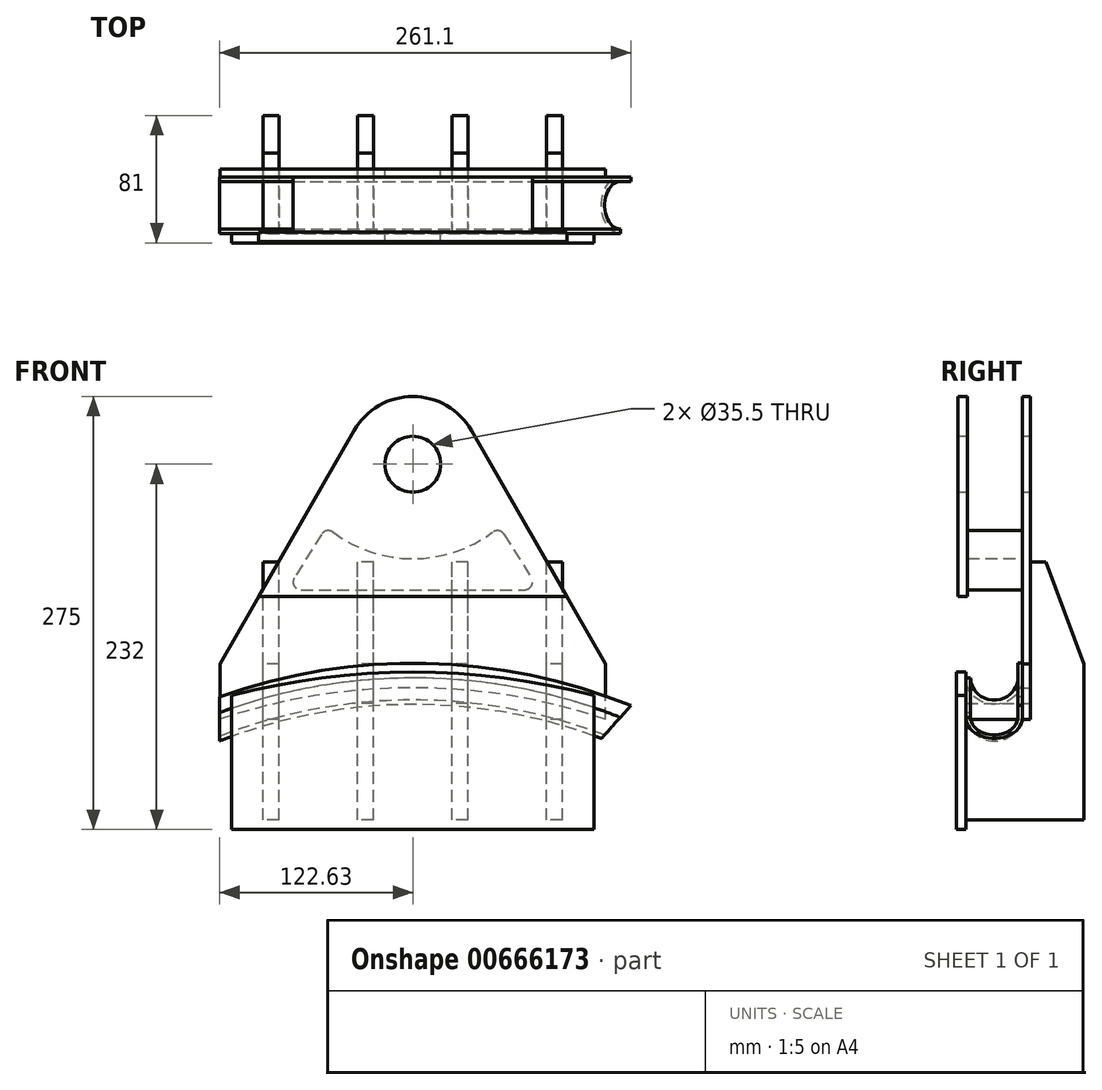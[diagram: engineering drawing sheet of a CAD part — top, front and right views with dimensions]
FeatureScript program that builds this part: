
annotation { "Feature Type Name" : "Feature", "Feature Type Description" : "" }
export const myFeature = defineFeature(function(context is Context, id is Id, definition is map)
    precondition{}
    {
        {
            var Q0;
            Q0=qCreatedBy(makeId("Front.planeOp"),FACE);
            var sketch = newSketch(context, id + "F0", { "sketchPlane" : qUnion([Q0])});
            skLineSegment(sketch, "E0", {"start": v(0, 0) * mm, "end": v(230, 0) * mm});
            skLineSegment(sketch, "E1", {"start": v(230, 0) * mm, "end": v(230, 85) * mm});
            skLineSegment(sketch, "E2", {"start": v(0, 0) * mm, "end": v(0, 85) * mm});
            skLineSegment(sketch, "E3", {"start": v(115, 0) * mm, "end": v(115, 100) * mm, "construction": true});
            skArc(sketch, "E4", {"start": v(230, 85) * mm, "mid": v(115, 100) * mm, "end": v(0, 85) * mm});
            skSolve(sketch);
        }
        {
            var Q0;
            Q0 = qSketchRegion(id + "F0", true);
            extrude(context, id + "F1", {"entities" : qUnion([Q0]), "oppositeDirection" : true, "depth" : 6 * mm, "offsetDistance" : 25 * mm});
        }
        {
            var Q0;
            Q0=qCreatedBy(makeId("Top.planeOp"),FACE);
            var sketch = newSketch(context, id + "F2", { "sketchPlane" : qUnion([Q0])});
            skLineSegment(sketch, "E5.0", {"start": v(0, 6) * mm, "end": v(230, 6) * mm});
            skLineSegment(sketch, "E6", {"start": v(0, 6) * mm, "end": v(0, 81) * mm});
            skLineSegment(sketch, "E7", {"start": v(0, 81) * mm, "end": v(230, 81) * mm});
            skLineSegment(sketch, "E8", {"start": v(230, 81) * mm, "end": v(230, 6) * mm});
            skSolve(sketch);
        }
        {
            var Q0;
            Q0 = qSketchRegion(id + "F2", true);
            extrude(context, id + "F3", {"entities" : qUnion([Q0]), "depth" : 230 * mm, "offsetDistance" : 25 * mm});
        }
        {
            var Q0;
            Q0=makeQuery(id+"F3.opExtrude","SWEPT_FACE",FACE,{"disambiguationData":[OSD([sQuery(id+"F2.wireOp",EDGE,"E6")])]});
            var sketch = newSketch(context, id + "F4", { "sketchPlane" : qUnion([Q0])});
            skLineSegment(sketch, "E9", {"start": v(-47, 230) * mm, "end": v(-47, 70) * mm});
            skLineSegment(sketch, "E10", {"start": v(-47, 70) * mm, "end": v(-6, 70) * mm});
            skLineSegment(sketch, "E11", {"start": v(-6, 70) * mm, "end": v(-6, 230) * mm});
            skLineSegment(sketch, "E12", {"start": v(-6, 230) * mm, "end": v(-47, 230) * mm});
            skSolve(sketch);
        }
        {
            var Q0;
            Q0 = qSketchRegion(id + "F4", true);
            extrude(context, id + "F5", {"entities" : qUnion([Q0]), "operationType" : NewBodyOperationType.REMOVE, "endBound" : BoundingType.THROUGH_ALL, "oppositeDirection" : true, "depth" : 25 * mm, "offsetDistance" : 25 * mm});
        }
        {
            var Q0;
            Q0=makeQuery(id+"F3.opExtrude","CAP_FACE",FACE,{"disambiguationData":[OSD([sQuery(id+"F2.wireOp",EDGE,"E5.0"),sQuery(id+"F2.wireOp",EDGE,"E6"),sQuery(id+"F2.wireOp",EDGE,"E7"),sQuery(id+"F2.wireOp",EDGE,"E8")])],"isStart":false});
            var sketch = newSketch(context, id + "F6", { "sketchPlane" : qUnion([Q0])});
            skLineSegment(sketch, "E13.0", {"start": v(230, 6) * mm, "end": v(0, 6) * mm, "construction": true});
            skLineSegment(sketch, "E14.bottom", {"start": v(0, 81) * mm, "end": v(20, 81) * mm});
            skLineSegment(sketch, "E14.top", {"start": v(0, 6) * mm, "end": v(20, 6) * mm});
            skLineSegment(sketch, "E14.left", {"start": v(0, 81) * mm, "end": v(0, 6) * mm});
            skLineSegment(sketch, "E14.right", {"start": v(20, 81) * mm, "end": v(20, 6) * mm});
            skLineSegment(sketch, "E15.bottom", {"start": v(30, 81) * mm, "end": v(80, 81) * mm});
            skLineSegment(sketch, "E15.top", {"start": v(30, 6) * mm, "end": v(80, 6) * mm});
            skLineSegment(sketch, "E15.left", {"start": v(30, 81) * mm, "end": v(30, 6) * mm});
            skLineSegment(sketch, "E15.right", {"start": v(80, 81) * mm, "end": v(80, 6) * mm});
            skLineSegment(sketch, "E16.bottom", {"start": v(90, 81) * mm, "end": v(140, 81) * mm});
            skLineSegment(sketch, "E16.top", {"start": v(90, 6) * mm, "end": v(140, 6) * mm});
            skLineSegment(sketch, "E16.left", {"start": v(90, 81) * mm, "end": v(90, 6) * mm});
            skLineSegment(sketch, "E16.right", {"start": v(140, 81) * mm, "end": v(140, 6) * mm});
            skLineSegment(sketch, "E17.bottom", {"start": v(150, 81) * mm, "end": v(200, 81) * mm});
            skLineSegment(sketch, "E17.top", {"start": v(150, 6) * mm, "end": v(200, 6) * mm});
            skLineSegment(sketch, "E17.left", {"start": v(150, 81) * mm, "end": v(150, 6) * mm});
            skLineSegment(sketch, "E17.right", {"start": v(200, 81) * mm, "end": v(200, 6) * mm});
            skLineSegment(sketch, "E18.bottom", {"start": v(210, 81) * mm, "end": v(230, 81) * mm});
            skLineSegment(sketch, "E18.top", {"start": v(210, 6) * mm, "end": v(230, 6) * mm});
            skLineSegment(sketch, "E18.left", {"start": v(210, 81) * mm, "end": v(210, 6) * mm});
            skLineSegment(sketch, "E18.right", {"start": v(230, 81) * mm, "end": v(230, 6) * mm});
            skSolve(sketch);
        }
        {
            var Q0;
            Q0 = qSketchRegion(id + "F6", true);
            extrude(context, id + "F7", {"entities" : qUnion([Q0]), "operationType" : NewBodyOperationType.REMOVE, "endBound" : BoundingType.THROUGH_ALL, "oppositeDirection" : true, "depth" : 25 * mm, "offsetDistance" : 25 * mm});
        }
        {
            var Q0;
            Q0=makeQuery(id+"F7.boolean.opBoolean","COPY",FACE,{"derivedFrom":makeQuery(id+"F7.opExtrude","SWEPT_FACE",FACE,{"disambiguationData":[OSD([sQuery(id+"F6.wireOp",EDGE,"E14.right")])]})});
            var sketch = newSketch(context, id + "F8", { "sketchPlane" : qUnion([Q0])});
            skLineSegment(sketch, "E19", {"start": v(-47, 170) * mm, "end": v(-47, 230) * mm});
            skLineSegment(sketch, "E20", {"start": v(-47, 230) * mm, "end": v(-81, 230) * mm});
            skLineSegment(sketch, "E21", {"start": v(-81, 230) * mm, "end": v(-81, 105) * mm});
            skLineSegment(sketch, "E22.0", {"start": v(-81, 0) * mm, "end": v(-6, 0) * mm, "construction": true});
            skLineSegment(sketch, "E23", {"start": v(-81, 105) * mm, "end": v(-57, 170) * mm});
            skLineSegment(sketch, "E24", {"start": v(-57, 170) * mm, "end": v(-47, 170) * mm});
            skLineSegment(sketch, "E25.bottom", {"start": v(-81, 0) * mm, "end": v(-6, 0) * mm});
            skLineSegment(sketch, "E25.top", {"start": v(-81, 6) * mm, "end": v(-6, 6) * mm});
            skLineSegment(sketch, "E25.left", {"start": v(-81, 0) * mm, "end": v(-81, 6) * mm});
            skLineSegment(sketch, "E25.right", {"start": v(-6, 0) * mm, "end": v(-6, 6) * mm});
            skSolve(sketch);
        }
        {
            var Q0;
            Q0=makeQuery(id+"F8.imprint","IMPRINT",FACE,{"disambiguationData":[TD([[makeQuery(id+"F8.imprint","IMPRINT",EDGE,{"derivedFrom":sQuery(id+"F8.wireOp",EDGE,"E19")}),1.0]])]});
            var Q1;
            Q1=makeQuery(id+"F8.imprint","IMPRINT",FACE,{"disambiguationData":[TD([[makeQuery(id+"F8.imprint","IMPRINT",EDGE,{"derivedFrom":sQuery(id+"F8.wireOp",EDGE,"E25.bottom")}),1.0]])]});
            extrude(context, id + "F9", {"entities" : qUnion([Q0, Q1]), "operationType" : NewBodyOperationType.REMOVE, "endBound" : BoundingType.THROUGH_ALL, "oppositeDirection" : true, "depth" : 25 * mm, "offsetDistance" : 25 * mm});
        }
        {
            var Q0;
            Q0=makeQuery(id+"F7.boolean.opBoolean","COPY",FACE,{"derivedFrom":makeQuery(id+"F7.opExtrude","SWEPT_FACE",FACE,{"disambiguationData":[OSD([sQuery(id+"F6.wireOp",EDGE,"E15.right")])]})});
            var sketch = newSketch(context, id + "F10", { "sketchPlane" : qUnion([Q0])});
            skLineSegment(sketch, "E26", {"start": v(-81, 190) * mm, "end": v(-57, 230) * mm});
            skLineSegment(sketch, "E27", {"start": v(-57, 230) * mm, "end": v(-81, 230) * mm});
            skLineSegment(sketch, "E28", {"start": v(-81, 230) * mm, "end": v(-81, 190) * mm});
            skSolve(sketch);
        }
        {
            var Q0;
            Q0 = qSketchRegion(id + "F10", true);
            extrude(context, id + "F11", {"entities" : qUnion([Q0]), "operationType" : NewBodyOperationType.REMOVE, "endBound" : BoundingType.THROUGH_ALL, "oppositeDirection" : true, "depth" : 25 * mm, "offsetDistance" : 25 * mm});
        }
        {
            var Q0;
            Q0=makeQuery(id+"F7.boolean.opBoolean","SPLIT",FACE,{"disambiguationData":[TD([makeQuery(id+"F7.opExtrude","SWEPT_FACE",FACE,{"disambiguationData":[OSD([sQuery(id+"F6.wireOp",EDGE,"E16.right")])]})])],"derivedFrom":makeQuery(id+"F5.boolean.opBoolean","COPY",FACE,{"derivedFrom":makeQuery(id+"F5.opExtrude","SWEPT_FACE",FACE,{"disambiguationData":[OSD([sQuery(id+"F4.wireOp",EDGE,"E9")])]})})});
            var sketch = newSketch(context, id + "F12", { "sketchPlane" : qUnion([Q0])});
            skLineSegment(sketch, "E29.0", {"start": v(0, 0) * mm, "end": v(230, 0) * mm, "construction": true});
            skLineSegment(sketch, "E30", {"start": v(115, 0) * mm, "end": v(115, 279.17) * mm, "construction": true});
            skLineSegment(sketch, "E31.0", {"start": v(237.5, -0.01) * mm, "end": v(237.5, 279.17) * mm, "construction": true});
            skLineSegment(sketch, "E32.0", {"start": v(-7.5, -0.01) * mm, "end": v(-7.5, 279.17) * mm, "construction": true});
            skLineSegment(sketch, "E33.0", {"start": v(-7.5, 70) * mm, "end": v(237.5, 70) * mm, "construction": true});
            skLineSegment(sketch, "E34.0", {"start": v(0, 90) * mm, "end": v(230, 90) * mm, "construction": true});
            skPoint(sketch, "E35", {"position": v(115, 90) * mm});
            skArc(sketch, "E36", {"start": v(237.5, 70) * mm, "mid": v(115, 90) * mm, "end": v(-7.5, 70) * mm});
            skLineSegment(sketch, "E37", {"start": v(-7.5, 70) * mm, "end": v(-7.5, 105) * mm});
            skLineSegment(sketch, "E38", {"start": v(237.5, 70) * mm, "end": v(237.5, 105) * mm});
            skCircle(sketch, "E39", {"center": v(115, 232) * mm, "radius": 17.75 * mm});
            skLineSegment(sketch, "E40.0", {"start": v(0, 275) * mm, "end": v(230, 275) * mm, "construction": true});
            skArc(sketch, "E41", {"start": v(152.3, 253.41) * mm, "mid": v(115, 275) * mm, "end": v(77.7, 253.41) * mm});
            skLineSegment(sketch, "E42", {"start": v(-7.5, 105) * mm, "end": v(77.7, 253.41) * mm});
            skLineSegment(sketch, "E43", {"start": v(237.5, 105) * mm, "end": v(152.3, 253.41) * mm});
            skSolve(sketch);
        }
        {
            var Q0;
            {var subQ12=sQuery(id+"F12.wireOp",EDGE,"E37");Q0=makeQuery(id+"F12.imprint","IMPRINT",FACE,{"disambiguationData":[TD([[makeQuery(id+"F12.imprint","IMPRINT",EDGE,{"derivedFrom":subQ12}),-1.0]])]});}
            var Q1;
            {var subQ0=sQuery(id+"F12.wireOp",EDGE,"E36");var subQ1=makeQuery(id+"F7.opExtrude","SWEPT_FACE",FACE,{"disambiguationData":[OSD([sQuery(id+"F6.wireOp",EDGE,"E17.left")])]});var subQ2=sQuery(id+"F4.wireOp",EDGE,"E9");var subQ3=makeQuery(id+"F5.boolean.opBoolean","COPY",FACE,{"derivedFrom":makeQuery(id+"F5.opExtrude","SWEPT_FACE",FACE,{"disambiguationData":[OSD([subQ2])]})});var subQ4=makeQuery(id+"F7.boolean.opBoolean","INTERSECT",EDGE,{"derivedFrom":[subQ3,subQ1]});var subQ5=makeQuery(id+"F12.imprint","INTERSECT",VERTEX,{"derivedFrom":[subQ4,subQ0]});Q1=makeQuery(id+"F12.imprint","IMPRINT",FACE,{"disambiguationData":[TD([[makeQuery(id+"F12.imprint","IMPRINT",EDGE,{"disambiguationData":[TD([[subQ5,-1.0]])],"derivedFrom":subQ0}),-1.0]])]});}
            extrude(context, id + "F13", {"entities" : qUnion([Q0, Q1]), "depth" : 5 * mm, "offsetDistance" : 25 * mm});
        }
        {
            var Q0;
            Q0=makeQuery(id+"F13.opExtrude","CAP_FACE",FACE,{"disambiguationData":[OSD([sQuery(id+"F12.wireOp",EDGE,"E36"),sQuery(id+"F12.wireOp",EDGE,"E37"),sQuery(id+"F12.wireOp",EDGE,"E38"),sQuery(id+"F12.wireOp",EDGE,"H9F1iutq-IefW-wYio-pTFB-sbYU66G88sGT"),sQuery(id+"F12.wireOp",EDGE,"E41"),sQuery(id+"F12.wireOp",EDGE,"E42"),sQuery(id+"F12.wireOp",EDGE,"E43")])],"isStart":false});
            var sketch = newSketch(context, id + "F14", { "sketchPlane" : qUnion([Q0])});
            skCircle(sketch, "E44", {"center": v(115, 257) * mm, "radius": 85 * mm, "construction": true});
            skLineSegment(sketch, "E45", {"start": v(115, 257) * mm, "end": v(115, 172) * mm, "construction": true});
            skLineSegment(sketch, "E46", {"start": v(115, 172) * mm, "end": v(-146.99, 172) * mm, "construction": true});
            skLineSegment(sketch, "E47", {"start": v(50.34, 172) * mm, "end": v(115, 172) * mm, "construction": true});
            skLineSegment(sketch, "E48", {"start": v(60, 192.2) * mm, "end": v(170, 192.2) * mm, "construction": true});
            skLineSegment(sketch, "E49.0", {"start": v(35, 152.2) * mm, "end": v(195, 152.2) * mm});
            skPoint(sketch, "E50", {"position": v(115, 152.2) * mm});
            skLineSegment(sketch, "E51", {"start": v(60, 192.2) * mm, "end": v(35, 152.2) * mm});
            skLineSegment(sketch, "E52", {"start": v(170, 192.2) * mm, "end": v(195, 152.2) * mm});
            skArc(sketch, "E53", {"start": v(60, 192.2) * mm, "mid": v(115, 172) * mm, "end": v(170, 192.2) * mm});
            skCircle(sketch, "E54.0", {"center": v(115, 232) * mm, "radius": 22.75 * mm, "construction": true});
            skSolve(sketch);
        }
        {
            var Q0;
            Q0 = qSketchRegion(id + "F14", true);
            extrude(context, id + "F15", {"entities" : qUnion([Q0]), "depth" : 35 * mm, "offsetDistance" : 25 * mm});
        }
        {
            var Q0;
            Q0=makeQuery(id+"F15.opExtrude","SWEPT_EDGE",EDGE,{"disambiguationData":[OSD([sQuery(id+"F14.wireOp",EDGE,"E51"),sQuery(id+"F14.wireOp",EDGE,"E53")])]});
            var Q1;
            Q1=makeQuery(id+"F15.opExtrude","SWEPT_EDGE",EDGE,{"disambiguationData":[OSD([sQuery(id+"F14.wireOp",EDGE,"E52"),sQuery(id+"F14.wireOp",EDGE,"E53")])]});
            var Q2;
            Q2=makeQuery(id+"F15.opExtrude","SWEPT_EDGE",EDGE,{"disambiguationData":[OSD([sQuery(id+"F14.wireOp",EDGE,"E49.0"),sQuery(id+"F14.wireOp",EDGE,"E51")])]});
            var Q3;
            Q3=makeQuery(id+"F15.opExtrude","SWEPT_EDGE",EDGE,{"disambiguationData":[OSD([sQuery(id+"F14.wireOp",EDGE,"E49.0"),sQuery(id+"F14.wireOp",EDGE,"E52")])]});
            fillet(context, id + "F16", {"entities" : qUnion([Q0, Q1, Q2, Q3]), "radius" : 5 * mm, "tangentPropagation" : true, "allowEdgeOverflow" : false});
        }
        {
            var Q0;
            Q0=makeQuery(id+"F15.opExtrude","CAP_FACE",FACE,{"disambiguationData":[OSD([sQuery(id+"F14.wireOp",EDGE,"E49.0"),sQuery(id+"F14.wireOp",EDGE,"E51"),sQuery(id+"F14.wireOp",EDGE,"E52"),sQuery(id+"F14.wireOp",EDGE,"E53")])],"isStart":false});
            var sketch = newSketch(context, id + "F17", { "sketchPlane" : qUnion([Q0])});
            skLineSegment(sketch, "E55.0", {"start": v(17.19, 148) * mm, "end": v(77.7, 253.41) * mm});
            skArc(sketch, "E55.1", {"start": v(152.3, 253.41) * mm, "mid": v(115, 275) * mm, "end": v(77.7, 253.41) * mm});
            skLineSegment(sketch, "E55.2", {"start": v(212.81, 148) * mm, "end": v(152.3, 253.41) * mm});
            skCircle(sketch, "E55.3", {"center": v(115, 232) * mm, "radius": 17.75 * mm});
            skLineSegment(sketch, "E56", {"start": v(17.19, 148) * mm, "end": v(212.81, 148) * mm});
            skPoint(sketch, "E57.orphan", {"position": v(-7.5, 105) * mm});
            skPoint(sketch, "E58.orphan", {"position": v(237.5, 105) * mm});
            skSolve(sketch);
        }
        {
            var Q0;
            Q0 = qSketchRegion(id + "F17", true);
            extrude(context, id + "F18", {"entities" : qUnion([Q0]), "depth" : 6 * mm, "offsetDistance" : 25 * mm});
        }
        {
            var Q0;
            Q0=makeQuery(id+"F7.boolean.opBoolean","SPLIT",FACE,{"disambiguationData":[TD([makeQuery(id+"F7.opExtrude","SWEPT_FACE",FACE,{"disambiguationData":[OSD([sQuery(id+"F6.wireOp",EDGE,"E15.right")])]})])],"derivedFrom":makeQuery(id+"F5.boolean.opBoolean","COPY",FACE,{"derivedFrom":makeQuery(id+"F5.opExtrude","SWEPT_FACE",FACE,{"disambiguationData":[OSD([sQuery(id+"F4.wireOp",EDGE,"E10")])]})})});
            var sketch = newSketch(context, id + "F19", { "sketchPlane" : qUnion([Q0])});
            skLineSegment(sketch, "E59.0", {"start": v(150, 6) * mm, "end": v(150, 47) * mm});
            skLineSegment(sketch, "E59.1", {"start": v(150, 47) * mm, "end": v(140, 47) * mm});
            skLineSegment(sketch, "E59.2", {"start": v(140, 6) * mm, "end": v(140, 47) * mm});
            skLineSegment(sketch, "E59.3", {"start": v(90, 6) * mm, "end": v(90, 47) * mm});
            skLineSegment(sketch, "E59.4", {"start": v(90, 47) * mm, "end": v(80, 47) * mm});
            skLineSegment(sketch, "E59.5", {"start": v(80, 6) * mm, "end": v(80, 47) * mm});
            skLineSegment(sketch, "E59.6", {"start": v(90, 6) * mm, "end": v(80, 6) * mm});
            skLineSegment(sketch, "E59.7", {"start": v(150, 6) * mm, "end": v(140, 6) * mm});
            skSolve(sketch);
        }
        {
            var Q0;
            Q0 = qSketchRegion(id + "F19", true);
            extrude(context, id + "F20", {"entities" : qUnion([Q0]), "operationType" : NewBodyOperationType.ADD, "depth" : 10 * mm, "offsetDistance" : 25 * mm});
        }
        {
            var Q0;
            Q0=makeQuery(id+"F13.opExtrude","CAP_FACE",FACE,{"disambiguationData":[OSD([sQuery(id+"F12.wireOp",EDGE,"E36"),sQuery(id+"F12.wireOp",EDGE,"E37"),sQuery(id+"F12.wireOp",EDGE,"E38"),sQuery(id+"F12.wireOp",EDGE,"H9F1iutq-IefW-wYio-pTFB-sbYU66G88sGT"),sQuery(id+"F12.wireOp",EDGE,"E41"),sQuery(id+"F12.wireOp",EDGE,"E42"),sQuery(id+"F12.wireOp",EDGE,"E43")])],"isStart":false});
            cPlane(context, id + "F21", {"entities" : qUnion([Q0]), "cplaneType" : CPlaneType.OFFSET, "offset" : 18 * mm, "width" : 150 * mm, "height" : 150 * mm});
        }
        {
            var Q0;
            Q0=qCreatedBy(id+"F21.planeOp",FACE);
            var sketch = newSketch(context, id + "F22", { "sketchPlane" : qUnion([Q0])});
            skArc(sketch, "E60", {"start": v(236.78, 60) * mm, "mid": v(114.5, 82.18) * mm, "end": v(-7.63, 59.21) * mm});
            skSolve(sketch);
        }
        {
            var Q0;
            Q0=sQuery(id+"F22.wireOp",VERTEX,"E60.end");
            var Q1;
            Q1=makeQuery(id+"F1.opExtrude","CAP_EDGE",EDGE,{"disambiguationData":[OSD([sQuery(id+"F0.wireOp",EDGE,"E0")])],"isStart":true});
            cPlane(context, id + "F23", {"entities" : qUnion([Q0, Q1]), "cplaneType" : CPlaneType.LINE_POINT, "offset" : 25 * mm, "width" : 150 * mm, "height" : 150 * mm});
        }
        {
            var Q0;
            Q0=qCreatedBy(id+"F23.planeOp",FACE);
            var sketch = newSketch(context, id + "F24", { "sketchPlane" : qUnion([Q0])});
            skLineSegment(sketch, "E61.0", {"start": v(24, 82.18) * mm, "end": v(24, 59.21) * mm, "construction": true});
            skArc(sketch, "E62", {"start": v(9, 74.21) * mm, "mid": v(24, 59.21) * mm, "end": v(39, 74.21) * mm});
            skArc(sketch, "E63.0", {"start": v(6, 74.21) * mm, "mid": v(29.2, 56.98) * mm, "end": v(39, 84.16) * mm});
            skLineSegment(sketch, "E64", {"start": v(42, 74.21) * mm, "end": v(6, 74.21) * mm, "construction": true});
            skPoint(sketch, "E65.orphan", {"position": v(46.04, 74.21) * mm});
            skLineSegment(sketch, "E66", {"start": v(42, 74.21) * mm, "end": v(42, 84.21) * mm});
            skLineSegment(sketch, "E67.0", {"start": v(39, 74.21) * mm, "end": v(39, 84.21) * mm});
            skLineSegment(sketch, "E68", {"start": v(42, 84.21) * mm, "end": v(39, 84.21) * mm});
            skLineSegment(sketch, "E69", {"start": v(6, 74.21) * mm, "end": v(9, 74.21) * mm});
            skSolve(sketch);
        }
        {
            var Q0;
            {var subQ1=sQuery(id+"F24.wireOp",EDGE,"E62");Q0=makeQuery(id+"F24.imprint","IMPRINT",FACE,{"disambiguationData":[TD([[makeQuery(id+"F24.imprint","IMPRINT",EDGE,{"derivedFrom":subQ1}),-1.0]])]});}
            var Q1;
            {var subQ3=sQuery(id+"F24.wireOp",EDGE,"E66");Q1=makeQuery(id+"F24.imprint","IMPRINT",FACE,{"disambiguationData":[TD([[makeQuery(id+"F24.imprint","IMPRINT",EDGE,{"derivedFrom":subQ3}),1.0]])]});}
            var Q2;
            Q2=sQuery(id+"F22.wireOp",EDGE,"E60");
            sweep(context, id + "F25", {"profiles" : qUnion([Q0, Q1]), "path" : qUnion([Q2])});
        }
    });
